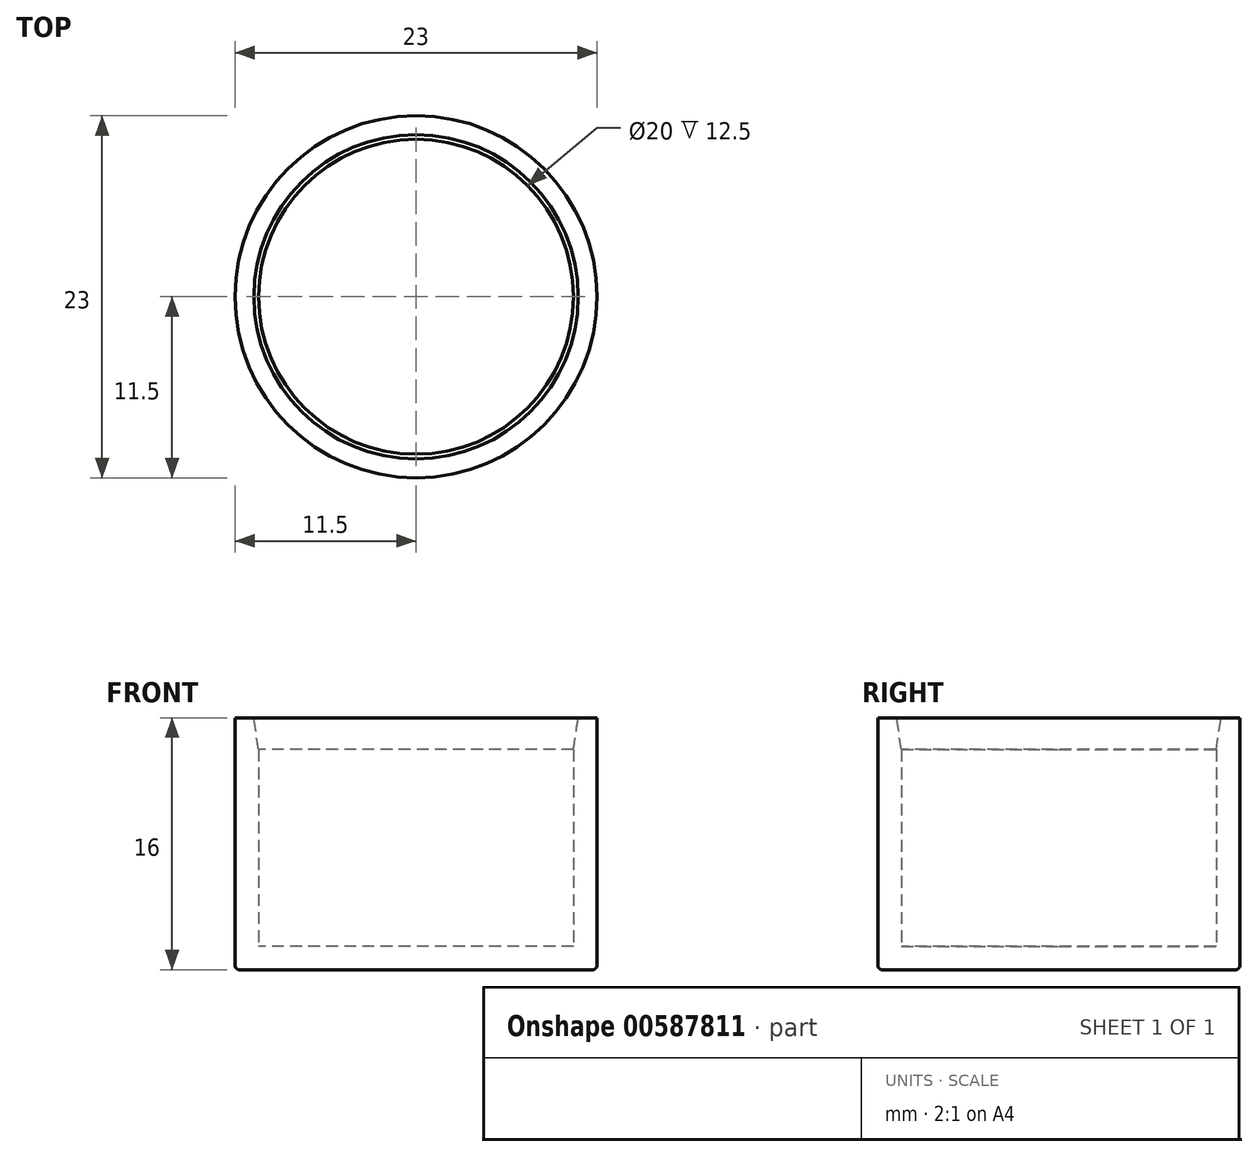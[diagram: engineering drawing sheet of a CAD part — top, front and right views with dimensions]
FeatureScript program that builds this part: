
annotation { "Feature Type Name" : "Feature", "Feature Type Description" : "" }
export const myFeature = defineFeature(function(context is Context, id is Id, definition is map)
    precondition{}
    {
        {
            assignVariable(context, id + "F0", {"name" : "T", "anyValue" : 1.5});
        }
        {
            assignVariable(context, id + "F1", {"name" : "H", "anyValue" : 16});
        }
        {
            var Q0;
            Q0=qCreatedBy(makeId("Top.planeOp"),FACE);
            var sketch = newSketch(context, id + "F2", { "sketchPlane" : qUnion([Q0])});
            skCircle(sketch, "E0", {"center": v(0, 0) * mm, "radius": 10 * mm});
            skCircle(sketch, "E1", {"center": v(0, 0) * mm, "radius": 11.5 * mm});
            skSolve(sketch);
        }
        {
            var Q0;
            Q0=makeQuery(id+"F2.imprint","IMPRINT",FACE,{"disambiguationData":[TD([[makeQuery(id+"F2.imprint","IMPRINT",EDGE,{"derivedFrom":sQuery(id+"F2.wireOp",EDGE,"E0")}),-1.0]])]});
            extrude(context, id + "F3", {"entities" : qUnion([Q0]), "depth" : getVariable(context, 'H') * mm, "offsetDistance" : 25 * mm});
        }
        {
            var Q0;
            Q0=makeQuery(id+"F2.imprint","IMPRINT",FACE,{"disambiguationData":[TD([[makeQuery(id+"F2.imprint","IMPRINT",EDGE,{"derivedFrom":sQuery(id+"F2.wireOp",EDGE,"E0")}),1.0]])]});
            extrude(context, id + "F4", {"entities" : qUnion([Q0]), "operationType" : NewBodyOperationType.ADD, "depth" : getVariable(context, 'T') * mm, "offsetDistance" : 25 * mm});
        }
        {
            var Q0;
            Q0=makeQuery(id+"F3.opExtrude","CAP_EDGE",EDGE,{"disambiguationData":[OSD([sQuery(id+"F2.wireOp",EDGE,"E1")])],"isStart":true});
            fillet(context, id + "F5", {"entities" : qUnion([Q0]), "radius" : 0.3 * mm, "tangentPropagation" : true, "allowEdgeOverflow" : false});
        }
        {
            var Q0;
            Q0=makeQuery(id+"F3.opExtrude","CAP_EDGE",EDGE,{"disambiguationData":[OSD([sQuery(id+"F2.wireOp",EDGE,"E0")])],"isStart":false});
            chamfer(context, id + "F6", {"entities" : qUnion([Q0]), "chamferType" : ChamferType.TWO_OFFSETS, "width1" : 2 * mm, "oppositeDirection" : false, "width2" : 0.3 * mm, "tangentPropagation" : true});
        }
    });
